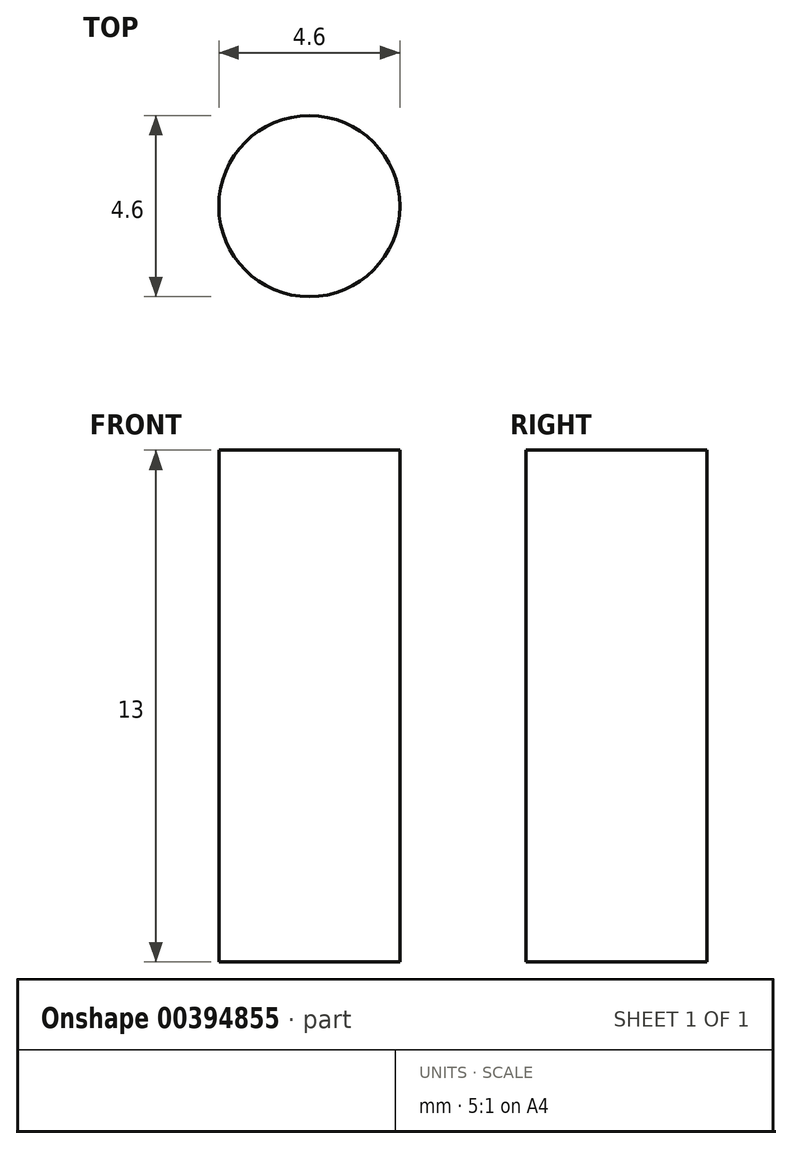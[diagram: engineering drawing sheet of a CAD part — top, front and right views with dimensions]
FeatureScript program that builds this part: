
annotation { "Feature Type Name" : "Feature", "Feature Type Description" : "" }
export const myFeature = defineFeature(function(context is Context, id is Id, definition is map)
    precondition{}
    {
        {
            var Q0;
            Q0=qCreatedBy(makeId("Front.planeOp"),FACE);
            var sketch = newSketch(context, id + "F0", { "sketchPlane" : qUnion([Q0])});
            skLineSegment(sketch, "E0", {"start": v(0, 0) * mm, "end": v(0, 13) * mm});
            skLineSegment(sketch, "E1", {"start": v(2.3, 0) * mm, "end": v(0, 0) * mm});
            skLineSegment(sketch, "E2", {"start": v(2.3, 0) * mm, "end": v(2.3, 13) * mm});
            skLineSegment(sketch, "E3", {"start": v(0, 13) * mm, "end": v(2.3, 13) * mm});
            skSolve(sketch);
        }
        {
            var Q0;
            Q0=makeQuery(id+"F0.imprint","IMPRINT",FACE,{"disambiguationData":[TD([[makeQuery(id+"F0.imprint","IMPRINT",EDGE,{"derivedFrom":sQuery(id+"F0.wireOp",EDGE,"E0")}),-1.0]])]});
            var Q1;
            Q1=sQuery(id+"F0.wireOp",EDGE,"E0");
            revolve(context, id + "F1", {"entities" : qUnion([Q0]), "axis" : qUnion([Q1]), "revolveType" : RevolveType.FULL});
        }
    });
